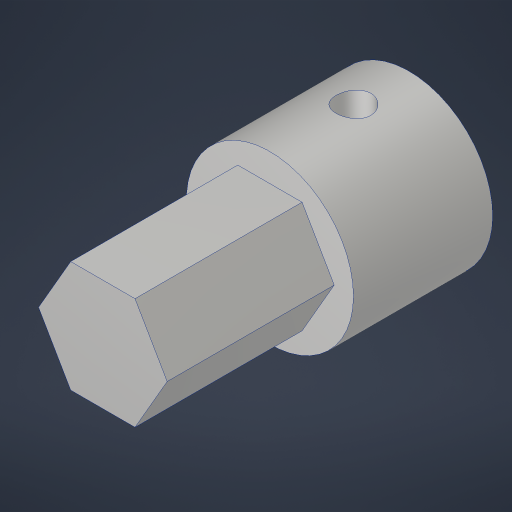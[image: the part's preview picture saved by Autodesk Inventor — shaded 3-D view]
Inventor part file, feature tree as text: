
AUTODESK INVENTOR PART (.ipt)
format: ipt  version: 2023.4 (Build 274418000, 418)  size: 184,320 bytes
history: native  units: in
note: dims shown in document units (in); Inventor stores cm internally (conversion verified against a paired STEP export)
features: sketch x3, extrude x2, hole x1
ambient origin geometry x8: Origin, YZ Plane, XZ Plane, XY Plane, X Axis, Y Axis, Z Axis, Center Point
bodies: Solid1 (feature_tree)
feature tree (6):
  extrude  "Extrusion1"  Depth=1.375in TaperAngle=0.0deg
  extrude  "Extrusion2"  Depth=0.75in TaperAngle=0.0deg
  hole  "Hole1"  [1 undecoded]
  sketch  "Sketch1"  dims[d0=0.75in d1=1.375in d2=0.0in]
  sketch  "Sketch2"  dims[d3=0.5in d4=0.75in d5=0.0in]
  sketch  "Sketch3"  dims[d6=0.25in d7=0.156in d8=0.38in d9=0.119in d10=0.25in d11=0.5635in d12=1.0in d13=0.8108in]
note: 1 required parameter value undecoded (feature->parameter linkage not recoverable at this tier; creation-order binding heuristic only, values carry confidence <= 0.55)
